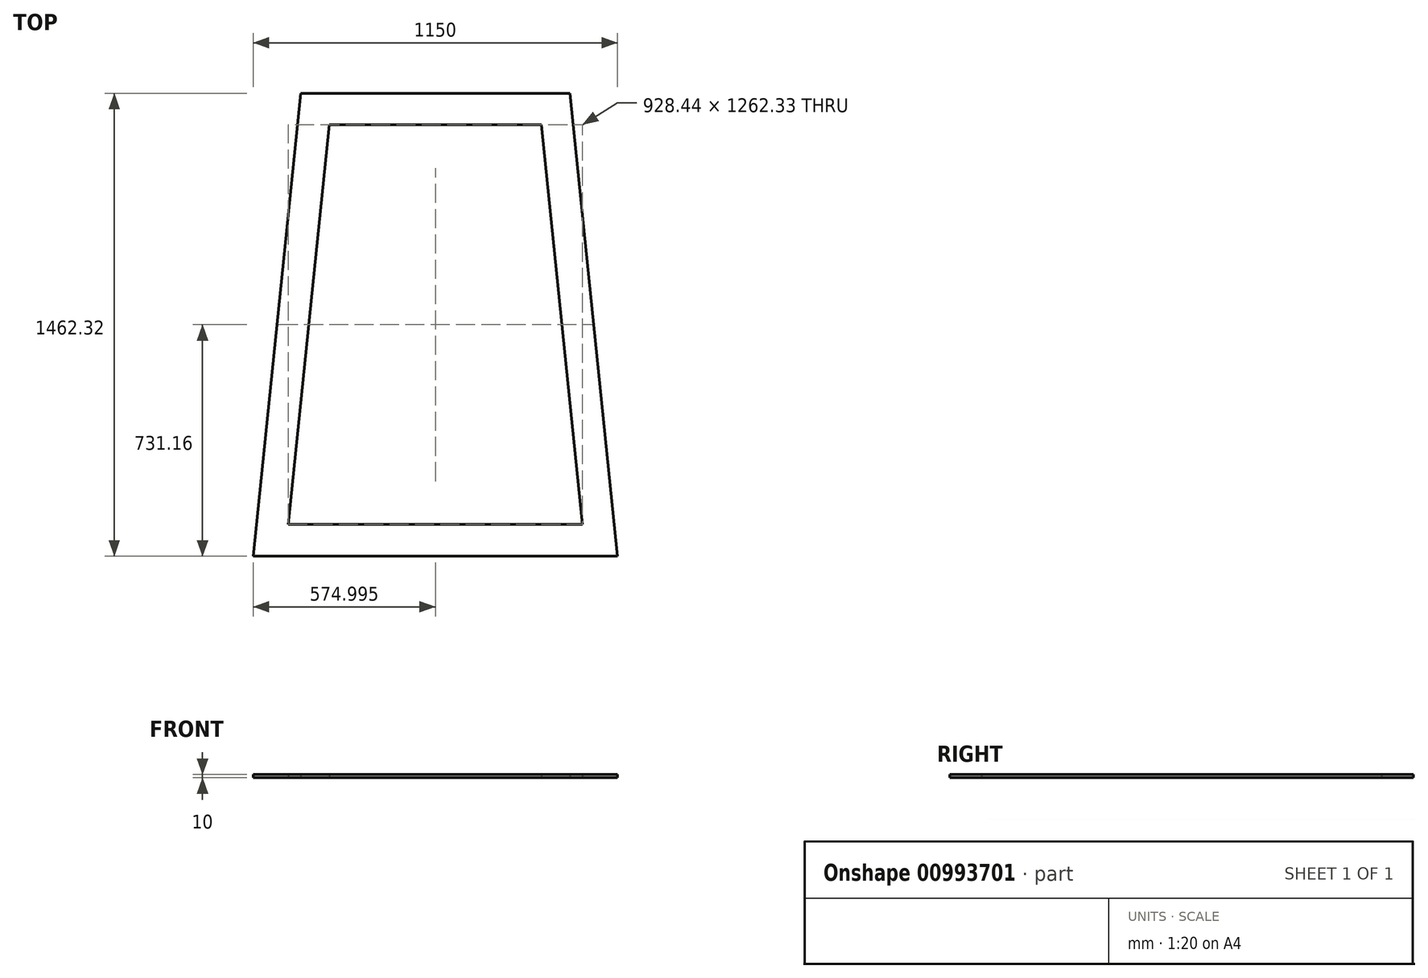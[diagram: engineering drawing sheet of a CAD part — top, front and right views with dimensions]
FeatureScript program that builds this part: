
annotation { "Feature Type Name" : "Feature", "Feature Type Description" : "" }
export const myFeature = defineFeature(function(context is Context, id is Id, definition is map)
    precondition{}
    {
        {
            var Q0;
            Q0=qCreatedBy(makeId("Top.planeOp"),FACE);
            var sketch = newSketch(context, id + "F0", { "sketchPlane" : qUnion([Q0])});
            skLineSegment(sketch, "E0", {"start": v(298.56, 47.57) * mm, "end": v(1148.56, 47.57) * mm});
            skLineSegment(sketch, "E1", {"start": v(298.56, 47.57) * mm, "end": v(148.56, -1414.75) * mm});
            skLineSegment(sketch, "E2", {"start": v(1148.56, 47.57) * mm, "end": v(1298.56, -1414.75) * mm});
            skLineSegment(sketch, "E3", {"start": v(1298.56, -1414.75) * mm, "end": v(148.56, -1414.75) * mm});
            skLineSegment(sketch, "E4", {"start": v(388.82, -52.43) * mm, "end": v(259.34, -1314.75) * mm});
            skLineSegment(sketch, "E5", {"start": v(259.34, -1314.75) * mm, "end": v(1187.77, -1314.75) * mm});
            skLineSegment(sketch, "E6", {"start": v(1187.77, -1314.75) * mm, "end": v(1058.29, -52.43) * mm});
            skLineSegment(sketch, "E7", {"start": v(1058.29, -52.43) * mm, "end": v(388.82, -52.43) * mm});
            skSolve(sketch);
        }
        {
            var Q0;
            Q0=makeQuery(id+"F0.imprint","IMPRINT",FACE,{"disambiguationData":[TD([[makeQuery(id+"F0.imprint","IMPRINT",EDGE,{"derivedFrom":sQuery(id+"F0.wireOp",EDGE,"E0")}),-1.0]])]});
            extrude(context, id + "F1", {"entities" : qUnion([Q0]), "depth" : 10 * mm, "offsetDistance" : 25 * mm});
        }
    });
